# Revit family: Lavatory-TOTO-Contemporary-Prominence-LPT242(G)
name_source: partatom
category: Plumbing Fixtures
revit_build: Autodesk Revit Architecture 2013 (Build: 20130531_2115(x64)
units: mm (PartAtom-declared; Revit-internal decimal feet)

## types (2) — shared parameters
04 CSI = 22 42 16
95 CSI = 15410
ADA Compliant = No
Assembly Code = D2010310
Basin Depth = 1' - 2 3/4"
Basin Width = 1' - 11 1/8"
Certifications = IAPMO(cUPC), State of Massachusetts, City of Los Angeles, and others
Code Compliance = UPC, IPC, NSPC, NPC Canada, and others
Cold Water Connection Radius = 0' - 0 1/4"
Cold Water Connector = Cold Water Connection
Color Availability = #01 Cotton, #03 Bone, #11 Colonial White, #12 Sedona Beige, #51 Ebony (not available in SanaGloss)
Default Elevation = 0' - 0"
Depth = 1' - 9 1/2"
Finish = Vitreous China - TOTO - 01 Cotton
Height = 2' - 10"
Hot Water Connection Radius = 0' - 0 1/4"
Hot Water Connector = Hot Water Connection
Industry Standards = Meets and exceeds ASME A112.19.2/CSA B45.1
Manufacturer = TOTO USA, Inc.
Manufacturer Fax = (770) 282-0002
Material = Vitreous china
Sanitary Connector = Sanitary Connection
Series = Prominence
Shipping Weight = 46.00 lb
Spec Sheet URL = http://assets.totousa.com
Style = Contemporary
Subcategory = Lavatories
Toto BIM Number = BM-00336
URL = http://www.totousa.com
Warranty = One Year Limited Warranty
Warranty URL = http://www.totousa.com
Waste Connection NPT Radius = 0' - 0 5/8"
Width = 2' - 2"

## per-type parameters (varying)
| type | Description | SanaGloss | ecoScorecard Product Page | ecoScorecard_data |
| LPT242 | Prominence® Pedestal Lavatory | No | http://toto.ecoscorecard.com | http://toto.ecoscorecard.com |
| LPT242G | Prominence® Pedestal Lavatory - with SanaGloss | Yes |  |  |

note: column(s) folded — value = type name in every type: Model

## geometry (parser evidence)
native form markers: Blend x4, Sweep x3
no freeform markers — native parametric forms only
